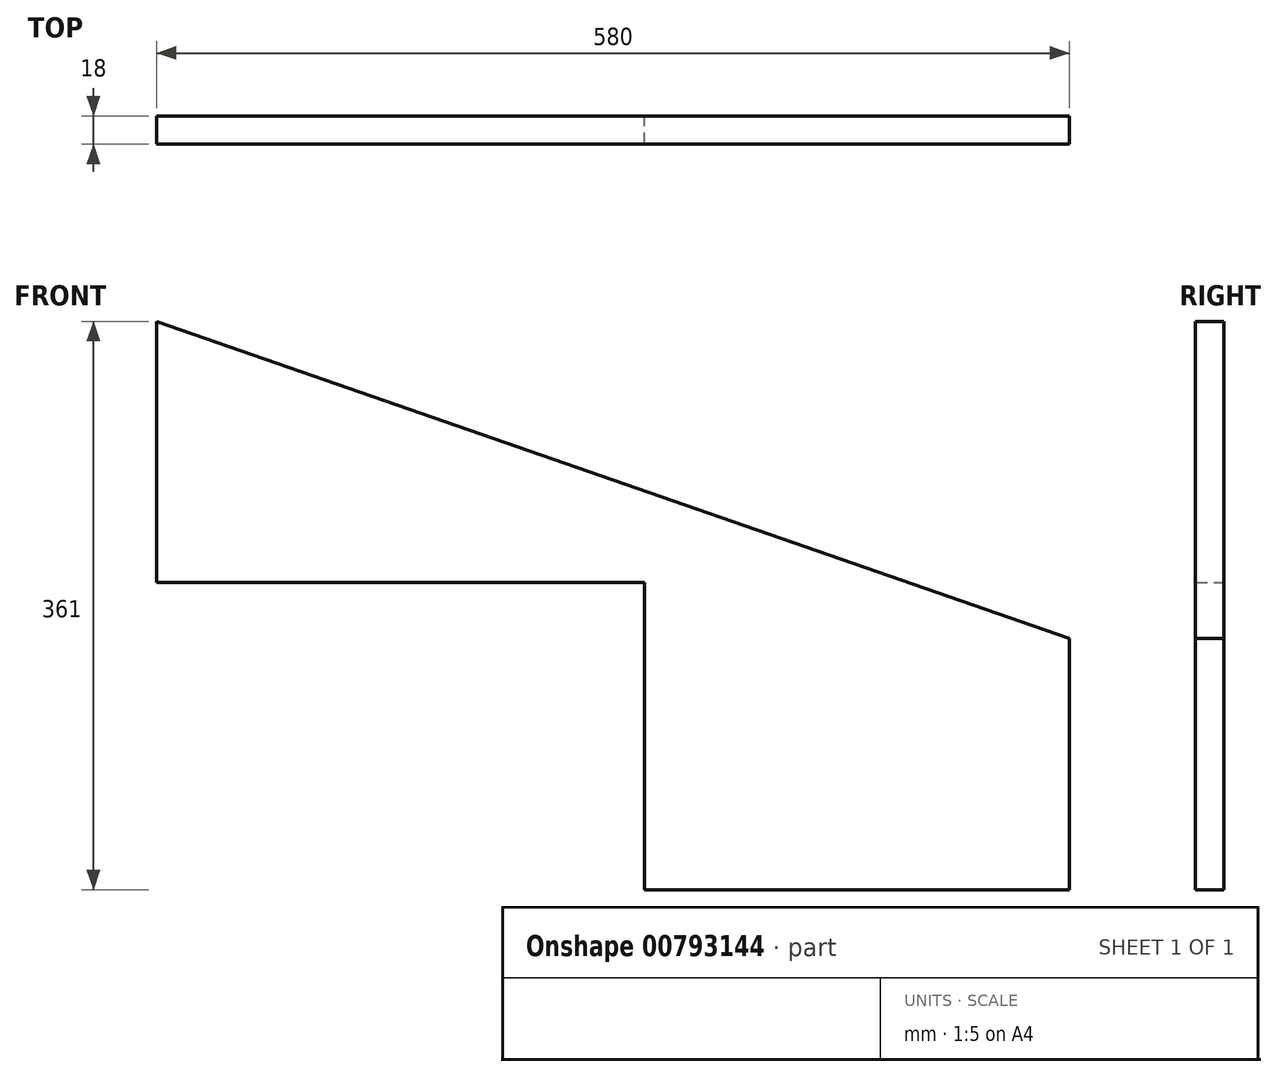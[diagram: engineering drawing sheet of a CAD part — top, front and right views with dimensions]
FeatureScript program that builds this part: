
annotation { "Feature Type Name" : "Feature", "Feature Type Description" : "" }
export const myFeature = defineFeature(function(context is Context, id is Id, definition is map)
    precondition{}
    {
        {
            var Q0;
            Q0=qCreatedBy(makeId("Front.planeOp"),FACE);
            var sketch = newSketch(context, id + "F0", { "sketchPlane" : qUnion([Q0])});
            skLineSegment(sketch, "E0", {"start": v(-62.58, 117) * mm, "end": v(-62.58, -49) * mm});
            skLineSegment(sketch, "E1", {"start": v(-62.58, -49) * mm, "end": v(247.42, -49) * mm});
            skLineSegment(sketch, "E2", {"start": v(247.42, -49) * mm, "end": v(247.42, -244) * mm});
            skLineSegment(sketch, "E3", {"start": v(247.42, -244) * mm, "end": v(517.42, -244) * mm});
            skLineSegment(sketch, "E4", {"start": v(517.42, -84.4) * mm, "end": v(517.42, -244) * mm});
            skLineSegment(sketch, "E5", {"start": v(517.42, -84.4) * mm, "end": v(-62.58, 117) * mm});
            skSolve(sketch);
        }
        {
            var Q0;
            Q0=makeQuery(id+"F0.imprint","IMPRINT",FACE,{"disambiguationData":[TD([[makeQuery(id+"F0.imprint","IMPRINT",EDGE,{"derivedFrom":sQuery(id+"F0.wireOp",EDGE,"E0")}),1.0]])]});
            extrude(context, id + "F1", {"entities" : qUnion([Q0]), "depth" : 18 * mm, "offsetDistance" : 25 * mm});
        }
    });
